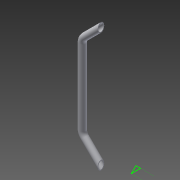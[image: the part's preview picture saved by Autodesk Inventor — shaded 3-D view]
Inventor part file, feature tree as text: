
AUTODESK INVENTOR PART (.ipt)
format: ipt  version: 2015 (Build 190159000, 159)  size: 137,728 bytes
history: native  units: mm
features: sketch x4, other x3, extrude x2, shell x1
ambient origin geometry x8: Origin, YZ Plane, XZ Plane, XY Plane, X Axis, Y Axis, Z Axis, Center Point
bodies: Body1 (feature_tree)
feature tree (10):
  other  "Bryła1"
  extrude  "Wyciągnięcie proste1"  Depth=20.0mm
  shell  "Skorupa1"  Thickness=430.0mm
  other  "Gięcie części1"
  other  "Gięcie części2"
  extrude  "Wyciągnięcie proste3"  Depth=2.0mm
  sketch  "Szkic1"
  sketch  "Szkic2"
  sketch  "Szkic3"
  sketch  "Szkic4"
